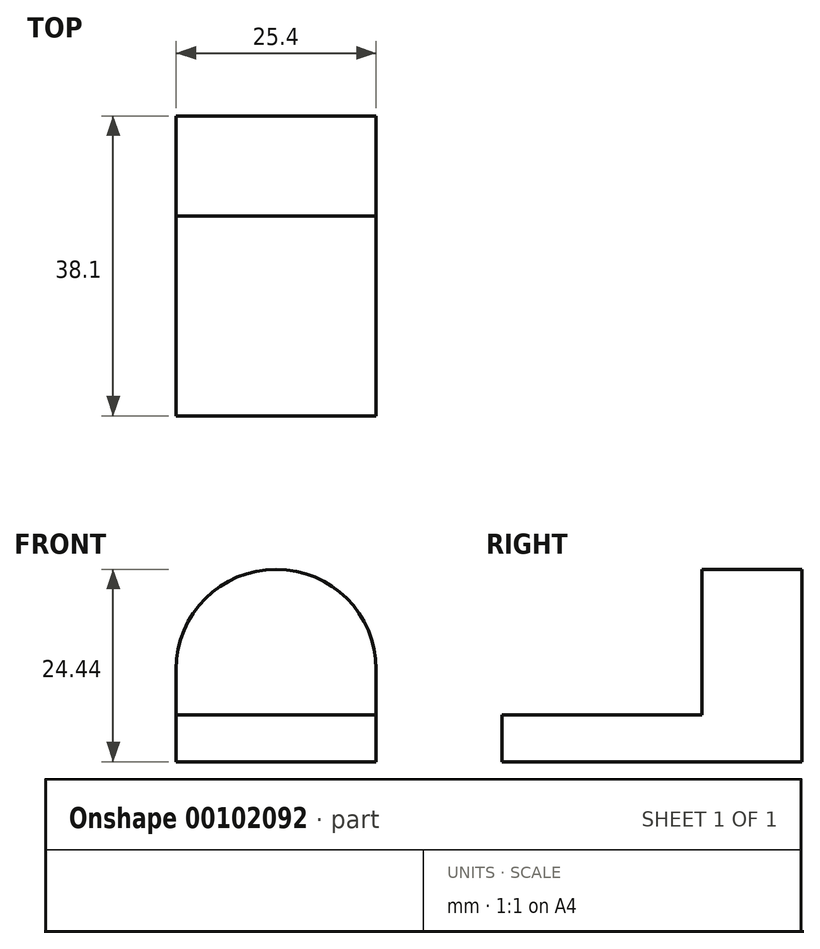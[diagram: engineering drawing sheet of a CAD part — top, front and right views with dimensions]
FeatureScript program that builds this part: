
annotation { "Feature Type Name" : "Feature", "Feature Type Description" : "" }
export const myFeature = defineFeature(function(context is Context, id is Id, definition is map)
    precondition{}
    {
        {
            var Q0;
            Q0=qCreatedBy(makeId("Front.planeOp"),FACE);
            var sketch = newSketch(context, id + "F0", { "sketchPlane" : qUnion([Q0])});
            skLineSegment(sketch, "E0", {"start": v(-25.4, 0) * mm, "end": v(0, 0) * mm});
            skLineSegment(sketch, "E1", {"start": v(0, 0) * mm, "end": v(0, 5.95) * mm});
            skLineSegment(sketch, "E2", {"start": v(0, 5.95) * mm, "end": v(-25.4, 5.95) * mm});
            skLineSegment(sketch, "E3", {"start": v(-25.4, 5.95) * mm, "end": v(-25.4, 0) * mm});
            skLineSegment(sketch, "E4", {"start": v(-25.4, 5.95) * mm, "end": v(-25.4, 11.74) * mm});
            skLineSegment(sketch, "E5", {"start": v(0, 5.95) * mm, "end": v(0, 11.74) * mm});
            skArc(sketch, "E6", {"start": v(0, 11.74) * mm, "mid": v(-12.7, 24.44) * mm, "end": v(-25.4, 11.74) * mm});
            skSolve(sketch);
        }
        {
            var Q0;
            Q0 = qSketchRegion(id + "F0", true);
            extrude(context, id + "F1", {"entities" : qUnion([Q0]), "oppositeDirection" : true, "depth" : 12.7 * mm});
        }
        {
            var Q0;
            Q0=makeQuery(id+"F0.imprint","IMPRINT",FACE,{"disambiguationData":[TD([[makeQuery(id+"F0.imprint","IMPRINT",EDGE,{"derivedFrom":sQuery(id+"F0.wireOp",EDGE,"E0")}),1.0]])]});
            extrude(context, id + "F2", {"entities" : qUnion([Q0]), "operationType" : NewBodyOperationType.ADD, "depth" : 25.4 * mm});
        }
    });
